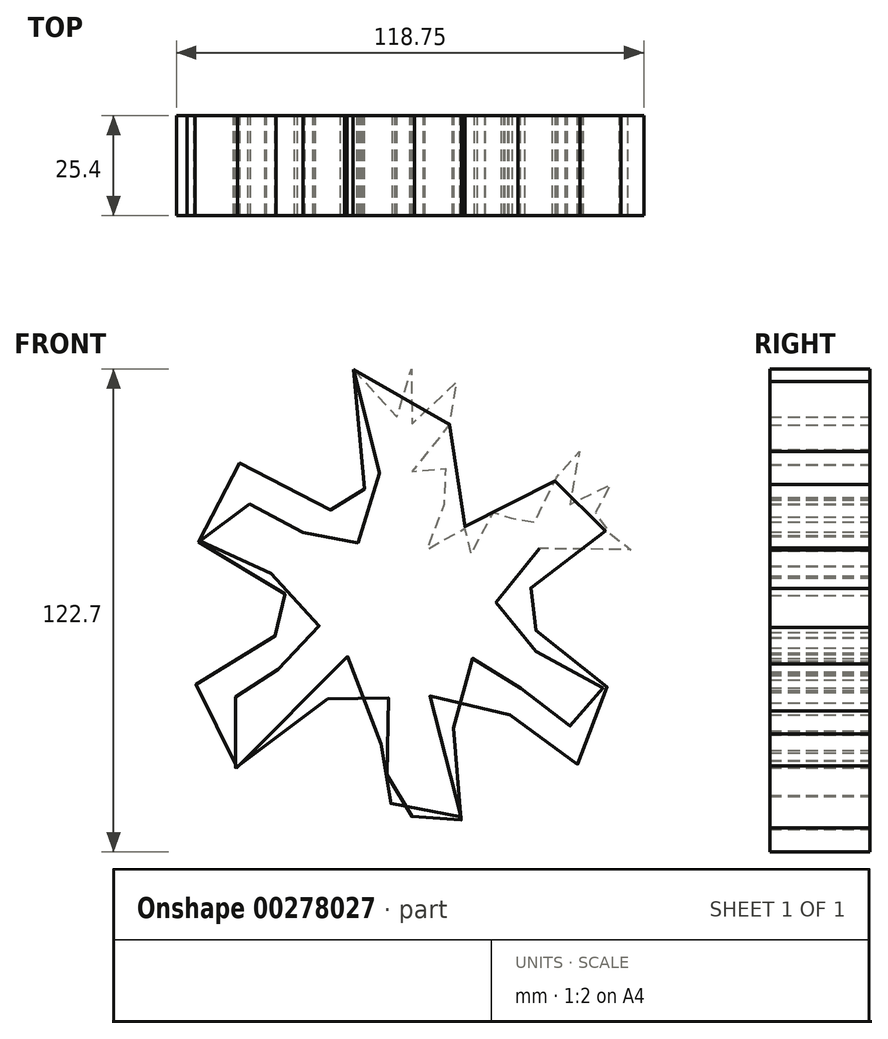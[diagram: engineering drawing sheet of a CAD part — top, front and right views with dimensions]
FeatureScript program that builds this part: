
annotation { "Feature Type Name" : "Feature", "Feature Type Description" : "" }
export const myFeature = defineFeature(function(context is Context, id is Id, definition is map)
    precondition{}
    {
        {
            var Q0;
            Q0=qCreatedBy(makeId("Front.planeOp"),FACE);
            var sketch = newSketch(context, id + "F0", { "sketchPlane" : qUnion([Q0])});
            skPoint(sketch, "E0.168.internal.snap0", {"position": v(-0.68, 45.55) * mm});
            skPoint(sketch, "E0.169.internal.snap0", {"position": v(-0.68, 45.55) * mm});
            skPoint(sketch, "E0.325.internal.snap0", {"position": v(-0.68, 45.55) * mm});
            skFitSpline(sketch, "E0", {"points": [v(-15.01, 45.55) * mm, v(-9.21, 37.7) * mm, v(-3.75, 33.6) * mm, v(-3.07, 38.73) * mm, v(-0.68, 45.55) * mm, v(0, 45.55) * mm, v(0, 37.02) * mm, v(0, 31.56) * mm, v(6.14, 36.34) * mm, v(11.6, 42.48) * mm, v(12.28, 38.38) * mm, v(10.24, 32.93) * mm, v(3.75, 26.1) * mm, v(0, 22.35) * mm, v(2.39, 12.8) * mm, v(8.19, 20.3) * mm, v(9.55, 21.32) * mm, v(9.9, 16.89) * mm, v(7.17, 10.4) * mm, v(3.41, 6.31) * mm, v(3.41, 0) * mm, v(9.55, 4.95) * mm, v(12.97, 6.65) * mm, v(12.28, 0) * mm, v(12.28, -4.26) * mm, v(15.7, 0) * mm, v(17.74, 2.9) * mm, v(19.45, 8.36) * mm, v(23.88, 11.09) * mm, v(26.61, 12.45) * mm, v(24.57, 7) * mm, v(23.54, 3.58) * mm, v(28.66, 5.29) * mm, v(33.1, 9.04) * mm, v(34.46, 12.8) * mm, v(36.85, 19.62) * mm, v(37.53, 22.35) * mm, v(40.6, 23.37) * mm, v(42.3, 24.74) * mm, v(40.94, 17.91) * mm, v(39.58, 11.43) * mm, v(44.01, 13.48) * mm, v(47.77, 15.87) * mm, v(50.84, 16.2) * mm, v(52.89, 13.82) * mm, v(48.45, 10.4) * mm, v(44.7, 8.36) * mm, v(43.33, 7.34) * mm, v(48.1, 4.95) * mm, v(52.54, 2.9) * mm, v(58.69, 0) * mm, v(52.2, 0) * mm, v(48.1, 0) * mm, v(44.36, 0) * mm, v(39.24, 0) * mm, v(37.2, 0) * mm, v(32.75, 0) * mm, v(29.68, 0) * mm, v(28.66, -3.92) * mm, v(32.75, -4.95) * mm, v(35.48, -5.97) * mm, v(31.73, -9.04) * mm, v(28.66, -10.07) * mm, v(25.25, -9.04) * mm, v(21.5, -8.36) * mm, v(18.77, -7.34) * mm, v(16.38, -9.38) * mm, v(19.1, -11.43) * mm, v(21.84, -14.16) * mm, v(23.2, -15.18) * mm, v(19.1, -18.25) * mm, v(17.06, -20.3) * mm, v(15.7, -20.98) * mm, v(18.42, -22.35) * mm, v(21.84, -22.35) * mm, v(24.57, -20.98) * mm, v(28.66, -19.96) * mm, v(31.73, -20.98) * mm, v(34.8, -22.69) * mm, v(36.17, -23.71) * mm, v(32.07, -25.76) * mm, v(29, -26.44) * mm, v(27.3, -26.78) * mm, v(30.03, -28.49) * mm, v(32.75, -30.54) * mm, v(36.5, -31.56) * mm, v(40.94, -30.88) * mm, v(45.72, -29.51) * mm, v(49.13, -29.17) * mm, v(52.54, -29.85) * mm, v(54.6, -31.22) * mm, v(53.9, -33.27) * mm, v(48.45, -35.31) * mm, v(45.38, -36) * mm, v(43, -37.02) * mm, v(44.7, -38.73) * mm, v(48.8, -40.1) * mm, v(50.5, -41.46) * mm, v(51.86, -42.82) * mm, v(52.54, -44.18) * mm, v(50.5, -46.91) * mm, v(47.77, -45.55) * mm, v(43.67, -43.5) * mm, v(41.28, -42.48) * mm, v(38.9, -41.11) * mm, v(40.26, -45.9) * mm, v(40.94, -49.3) * mm, v(41.63, -53.4) * mm, v(41.63, -55.1) * mm, v(37.87, -53.74) * mm, v(36.85, -53.74) * mm, v(36.85, -51.7) * mm, v(36.17, -47.6) * mm, v(34.8, -44.87) * mm, v(34.12, -42.14) * mm, v(33.44, -38.73) * mm, v(31.39, -36) * mm, v(29.34, -36) * mm, v(27.3, -35.31) * mm, v(25.25, -33.27) * mm, v(22.52, -32.24) * mm, v(24.22, -35.31) * mm, v(24.22, -38.04) * mm, v(24.57, -40.1) * mm, v(25.25, -42.14) * mm, v(21.15, -40.77) * mm, v(18.42, -39.4) * mm, v(18.42, -37.36) * mm, v(17.74, -33.95) * mm, v(17.06, -31.22) * mm, v(16.38, -29.17) * mm, v(15.7, -28.15) * mm, v(13.99, -27.12) * mm, v(12.28, -26.44) * mm, v(12.28, -28.15) * mm, v(12.28, -30.88) * mm, v(11.6, -32.93) * mm, v(10.24, -36.34) * mm, v(7.85, -35.31) * mm, v(5.12, -33.95) * mm, v(3.75, -33.27) * mm, v(3.07, -34.97) * mm, v(4.78, -38.04) * mm, v(6.48, -41.8) * mm, v(8.19, -42.82) * mm, v(10.24, -44.87) * mm, v(10.24, -48.96) * mm, v(10.24, -51.7) * mm, v(6.82, -50.33) * mm, v(5.8, -48.28) * mm, v(4.78, -47.6) * mm, v(3.75, -46.23) * mm, v(3.07, -53.74) * mm, v(3.41, -57.15) * mm, v(6.14, -59.88) * mm, v(8.19, -62.6) * mm, v(11.26, -64.32) * mm, v(12.28, -67.39) * mm, v(11.6, -70.8) * mm, v(8.87, -68.75) * mm, v(5.8, -66.7) * mm, v(4.1, -64.32) * mm, v(0, -62.95) * mm, v(0, -65.34) * mm, v(0, -70.46) * mm, v(0, -76.2) * mm, v(-4.1, -76.2) * mm, v(-4.44, -71.14) * mm, v(-0.68, -68.75) * mm, v(-0.68, -65.34) * mm, v(-3.75, -62.6) * mm, v(-5.12, -63.97) * mm, v(-7.85, -67.39) * mm, v(-9.21, -68.75) * mm, v(-11.6, -70.8) * mm, v(-12.97, -71.14) * mm, v(-15.01, -69.43) * mm, v(-14.67, -66.36) * mm, v(-11.6, -64.32) * mm, v(-9.55, -61.93) * mm, v(-7.85, -59.88) * mm, v(-6.82, -58.17) * mm, v(-6.14, -56.47) * mm, v(-4.78, -55.44) * mm, v(-4.1, -54.08) * mm, v(-4.1, -51.7) * mm, v(-4.78, -49.64) * mm, v(-5.12, -46.23) * mm, v(-5.8, -46.91) * mm, v(-9.55, -50.67) * mm, v(-11.6, -51) * mm, v(-12.28, -48.28) * mm, v(-11.6, -46.23) * mm, v(-9.21, -43.84) * mm, v(-8.19, -40.77) * mm, v(-6.82, -38.73) * mm, v(-5.12, -36.34) * mm, v(-4.44, -33.6) * mm, v(-5.46, -31.22) * mm, v(-10.58, -35.31) * mm, v(-13.65, -36) * mm, v(-13.65, -33.6) * mm, v(-13.65, -29.85) * mm, v(-14.67, -25.08) * mm, v(-16.38, -27.12) * mm, v(-17.74, -28.49) * mm, v(-18.77, -33.27) * mm, v(-21.84, -38.38) * mm, v(-24.22, -41.46) * mm, v(-27.3, -41.8) * mm, v(-25.59, -37.36) * mm, v(-25.25, -35.31) * mm, v(-29.34, -37.36) * mm, v(-32.07, -39.07) * mm, v(-34.8, -39.4) * mm, v(-37.2, -44.87) * mm, v(-37.53, -50.33) * mm, v(-38.9, -52.71) * mm, v(-45.38, -55.44) * mm, v(-44.36, -51.7) * mm, v(-43.67, -48.62) * mm, v(-42.65, -45.55) * mm, v(-41.97, -42.14) * mm, v(-46.4, -44.87) * mm, v(-50.5, -46.23) * mm, v(-55.27, -46.91) * mm, v(-54.6, -43.5) * mm, v(-52.54, -42.82) * mm, v(-48.45, -40.1) * mm, v(-45.04, -37.7) * mm, v(-47.43, -36.68) * mm, v(-51.18, -36) * mm, v(-56.64, -33.95) * mm, v(-60.05, -32.58) * mm, v(-57.32, -29.17) * mm, v(-54.93, -27.8) * mm, v(-51.18, -28.83) * mm, v(-47.08, -28.49) * mm, v(-43, -30.54) * mm, v(-37.53, -31.9) * mm, v(-34.12, -30.54) * mm, v(-31.39, -28.15) * mm, v(-30.03, -26.78) * mm, v(-34.46, -26.78) * mm, v(-36.5, -26.44) * mm, v(-37.53, -25.42) * mm, v(-36.17, -23.37) * mm, v(-34.12, -21.67) * mm, v(-27.98, -21.32) * mm, v(-23.54, -22.35) * mm, v(-20.47, -22.35) * mm, v(-18.42, -21.67) * mm, v(-22.18, -20.3) * mm, v(-25.25, -18.25) * mm, v(-25.25, -17.23) * mm, v(-23.88, -13.48) * mm, v(-22.18, -13.14) * mm, v(-19.1, -11.09) * mm, v(-17.4, -9.72) * mm, v(-20.13, -7) * mm, v(-24.57, -8.02) * mm, v(-31.05, -10.75) * mm, v(-34.8, -11.43) * mm, v(-35.83, -8.02) * mm, v(-37.2, -7.68) * mm, v(-34.8, -5.29) * mm, v(-31.39, -4.26) * mm, v(-29.34, -2.9) * mm, v(-31.73, 0) * mm, v(-36.5, 0) * mm, v(-39.24, 0) * mm, v(-42.65, 0) * mm, v(-46.4, 0) * mm, v(-50.16, 0) * mm, v(-52.54, 0) * mm, v(-55.27, 0) * mm, v(-57.32, 0) * mm, v(-52.2, 2.9) * mm, v(-49.81, 3.92) * mm, v(-47.08, 4.95) * mm, v(-44.36, 5.97) * mm, v(-44.36, 7.68) * mm, v(-51.18, 8.36) * mm, v(-51.86, 9.72) * mm, v(-55.27, 12.8) * mm, v(-54.6, 14.5) * mm, v(-53.57, 16.2) * mm, v(-47.08, 15.52) * mm, v(-44.7, 13.82) * mm, v(-41.28, 11.43) * mm, v(-43, 15.87) * mm, v(-43.67, 20.64) * mm, v(-44.36, 23.03) * mm, v(-44.01, 25.08) * mm, v(-39.92, 24.05) * mm, v(-38.21, 19.62) * mm, v(-35.83, 15.52) * mm, v(-34.8, 11.09) * mm, v(-34.8, 7.68) * mm, v(-32.07, 6.31) * mm, v(-27.98, 4.26) * mm, v(-24.9, 3.24) * mm, v(-25.25, 5.63) * mm, v(-27.3, 9.72) * mm, v(-27.64, 12.45) * mm, v(-23.88, 11.77) * mm, v(-20.81, 9.72) * mm, v(-19.1, 5.63) * mm, v(-16.72, 0) * mm, v(-17.06, -3.24) * mm, v(-13.65, -4.26) * mm, v(-13.65, 0) * mm, v(-13.65, 4.26) * mm, v(-7.17, 0) * mm, v(-4.78, 0) * mm, v(-4.44, 5.63) * mm, v(-5.8, 7.68) * mm, v(-9.55, 9.04) * mm, v(-11.26, 10.75) * mm, v(-12.28, 12.8) * mm, v(-12.28, 15.18) * mm, v(-12.62, 18.25) * mm, v(-12.28, 21.32) * mm, v(-8.19, 18.94) * mm, v(-5.12, 14.84) * mm, v(-0.68, 13.14) * mm, v(-4.1, 18.25) * mm, v(-4.1, 24.74) * mm, v(-5.46, 27.47) * mm, v(-8.19, 30.54) * mm, v(-12.28, 33.6) * mm, v(-15.01, 37.02) * mm, v(-15.01, 41.46) * mm, v(-15.01, 45.55) * mm]});
            skSolve(sketch);
        }
        {
            var Q0;
            Q0=makeQuery(id+"F0.imprint","IMPRINT",FACE,{"disambiguationData":[TD([[makeQuery(id+"F0.imprint","IMPRINT",EDGE,{"derivedFrom":sQuery(id+"F0.wireOp",EDGE,"E0")}),-1.0]])]});
            extrude(context, id + "F1", {"entities" : qUnion([Q0]), "depth" : 25.4 * mm});
        }
    });
